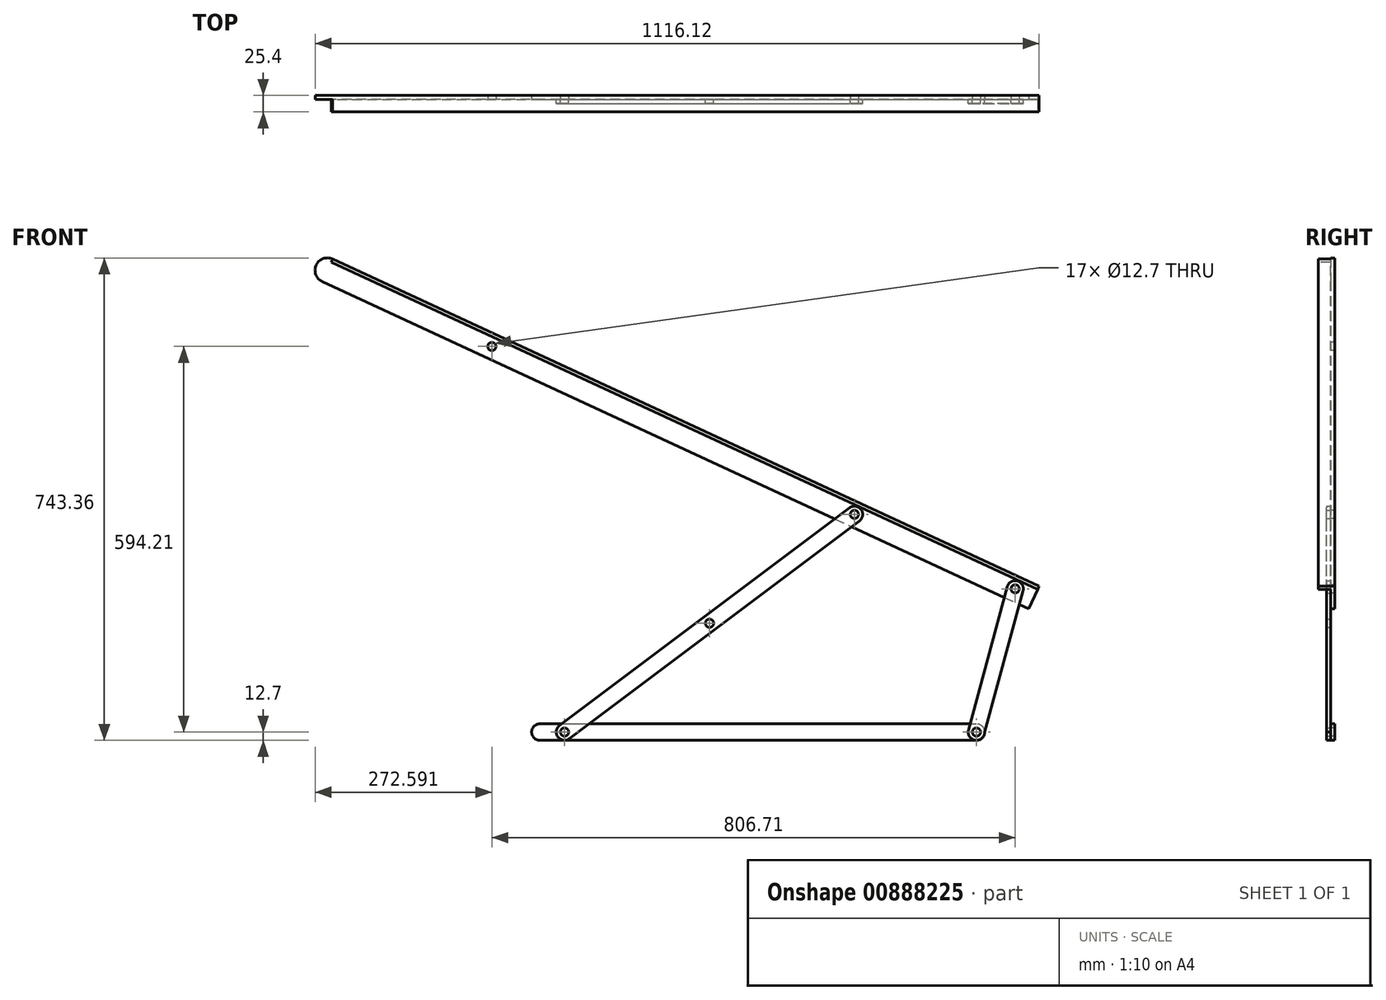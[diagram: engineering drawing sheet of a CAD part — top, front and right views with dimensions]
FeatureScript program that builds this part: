
annotation { "Feature Type Name" : "Feature", "Feature Type Description" : "" }
export const myFeature = defineFeature(function(context is Context, id is Id, definition is map)
    precondition{}
    {
        {
            var Q0;
            Q0=qCreatedBy(makeId("Front.planeOp"),FACE);
            var sketch = newSketch(context, id + "F0", { "sketchPlane" : qUnion([Q0])});
            skCircle(sketch, "E0", {"center": v(0, 0) * mm, "radius": 6.35 * mm});
            skCircle(sketch, "E1", {"center": v(0, 0) * mm, "radius": 12.7 * mm});
            skLineSegment(sketch, "E2", {"start": v(0, 0) * mm, "end": v(-673.1, 0) * mm, "construction": true});
            skCircle(sketch, "E3", {"center": v(-673.1, 0) * mm, "radius": 12.7 * mm});
            skLineSegment(sketch, "E4", {"start": v(-673.1, 12.7) * mm, "end": v(0, 12.7) * mm});
            skLineSegment(sketch, "E5", {"start": v(-673.1, -12.7) * mm, "end": v(0, -12.7) * mm});
            skCircle(sketch, "E6", {"center": v(-635, 0) * mm, "radius": 6.35 * mm});
            skCircle(sketch, "E7", {"center": v(59.73, 220.66) * mm, "radius": 12.7 * mm});
            skCircle(sketch, "E8", {"center": v(-188.04, 335.4) * mm, "radius": 12.7 * mm});
            skCircle(sketch, "E9", {"center": v(-1000.52, 711.61) * mm, "radius": 19.05 * mm});
            skLineSegment(sketch, "E10", {"start": v(-635, 0) * mm, "end": v(-188.04, 335.4) * mm, "construction": true});
            skLineSegment(sketch, "E11", {"start": v(0, 0) * mm, "end": v(59.73, 220.66) * mm, "construction": true});
            skLineSegment(sketch, "E12", {"start": v(59.73, 220.66) * mm, "end": v(-1000.52, 711.61) * mm, "construction": true});
            skCircle(sketch, "E13", {"center": v(-746.98, 594.21) * mm, "radius": 6.35 * mm});
            skCircle(sketch, "E14", {"center": v(-411.52, 167.7) * mm, "radius": 6.35 * mm});
            skCircle(sketch, "E15", {"center": v(-188.04, 335.4) * mm, "radius": 6.35 * mm});
            skCircle(sketch, "E16", {"center": v(59.73, 220.66) * mm, "radius": 6.35 * mm});
            skCircle(sketch, "E17", {"center": v(-635, 0) * mm, "radius": 12.7 * mm});
            skLineSegment(sketch, "E18", {"start": v(-642.62, 10.16) * mm, "end": v(-195.67, 345.55) * mm});
            skLineSegment(sketch, "E19", {"start": v(12.7, 0) * mm, "end": v(71.98, 217.32) * mm});
            skLineSegment(sketch, "E20", {"start": v(47.47, 223.98) * mm, "end": v(-12.26, 3.32) * mm});
            skLineSegment(sketch, "E21", {"start": v(96.55, 224.6) * mm, "end": v(-992.51, 728.9) * mm});
            skLineSegment(sketch, "E22", {"start": v(-1008.52, 694.33) * mm, "end": v(80.54, 190.03) * mm});
            skLineSegment(sketch, "E23", {"start": v(80.54, 190.03) * mm, "end": v(96.55, 224.6) * mm});
            skLineSegment(sketch, "E24", {"start": v(-627.38, -10.16) * mm, "end": v(-180.42, 325.23) * mm});
            skSolve(sketch);
        }
        {
            var Q0;
            {var subQ3=sQuery(id+"F0.wireOp",EDGE,"E5");var subQ5=sQuery(id+"F0.wireOp",EDGE,"E1");var subQ6=makeQuery(id+"F0.imprint","INTERSECT",VERTEX,{"derivedFrom":[subQ5,subQ3]});Q0=makeQuery(id+"F0.imprint","IMPRINT",FACE,{"disambiguationData":[TD([[makeQuery(id+"F0.imprint","IMPRINT",EDGE,{"disambiguationData":[TD([[subQ6,1.0]])],"derivedFrom":subQ5}),-1.0]])]});}
            var Q1;
            {var subQ0=sQuery(id+"F0.wireOp",EDGE,"E3");var subQ1=makeQuery(id+"F0.imprint","INTERSECT",VERTEX,{"derivedFrom":[subQ0,sQuery(id+"F0.wireOp",EDGE,"E4")]});Q1=makeQuery(id+"F0.imprint","IMPRINT",FACE,{"disambiguationData":[TD([[makeQuery(id+"F0.imprint","IMPRINT",EDGE,{"disambiguationData":[TD([[subQ1,-1.0]])],"derivedFrom":subQ0}),1.0]])]});}
            var Q2;
            {var subQ1=sQuery(id+"F0.wireOp",EDGE,"E3");var subQ5=sQuery(id+"F0.wireOp",EDGE,"E4");var subQ8=makeQuery(id+"F0.imprint","INTERSECT",VERTEX,{"derivedFrom":[subQ1,subQ5]});Q2=makeQuery(id+"F0.imprint","IMPRINT",FACE,{"disambiguationData":[TD([[makeQuery(id+"F0.imprint","IMPRINT",EDGE,{"disambiguationData":[TD([[subQ8,1.0]])],"derivedFrom":subQ1}),-1.0]])]});}
            var Q3;
            Q3=makeQuery(id+"F0.imprint","IMPRINT",FACE,{"disambiguationData":[TD([[makeQuery(id+"F0.imprint","IMPRINT",EDGE,{"derivedFrom":sQuery(id+"F0.wireOp",EDGE,"E6")}),-1.0]])]});
            var Q4;
            {var subQ0=sQuery(id+"F0.wireOp",EDGE,"E10");var subQ1=sQuery(id+"F0.wireOp",EDGE,"E4");var subQ2=makeQuery(id+"F0.imprint","INTERSECT",VERTEX,{"derivedFrom":[subQ1,subQ0]});Q4=makeQuery(id+"F0.imprint","IMPRINT",FACE,{"disambiguationData":[TD([[makeQuery(id+"F0.imprint","IMPRINT",EDGE,{"disambiguationData":[TD([[subQ2,-1.0]])],"derivedFrom":subQ1}),-1.0]])]});}
            var Q5;
            {var subQ0=sQuery(id+"F0.wireOp",EDGE,"E17");var subQ1=sQuery(id+"F0.wireOp",EDGE,"E4");var subQ2=makeQuery(id+"F0.imprint","INTERSECT",VERTEX,{"derivedFrom":[subQ1,subQ0]});Q5=makeQuery(id+"F0.imprint","IMPRINT",FACE,{"disambiguationData":[TD([[makeQuery(id+"F0.imprint","IMPRINT",EDGE,{"disambiguationData":[TD([[subQ2,-1.0]])],"derivedFrom":subQ1}),-1.0]])]});}
            var Q6;
            {var subQ0=sQuery(id+"F0.wireOp",EDGE,"E20");var subQ1=sQuery(id+"F0.wireOp",EDGE,"E1");var subQ2=makeQuery(id+"F0.imprint","INTERSECT",VERTEX,{"derivedFrom":[subQ1,subQ0]});Q6=makeQuery(id+"F0.imprint","IMPRINT",FACE,{"disambiguationData":[TD([[makeQuery(id+"F0.imprint","IMPRINT",EDGE,{"disambiguationData":[TD([[subQ2,1.0]])],"derivedFrom":subQ1}),-1.0]])]});}
            var Q7;
            Q7=makeQuery(id+"F0.imprint","IMPRINT",FACE,{"disambiguationData":[TD([[makeQuery(id+"F0.imprint","IMPRINT",EDGE,{"derivedFrom":sQuery(id+"F0.wireOp",EDGE,"E0")}),-1.0]])]});
            var Q8;
            {var subQ0=sQuery(id+"F0.wireOp",EDGE,"E19");var subQ1=sQuery(id+"F0.wireOp",EDGE,"E7");var subQ2=makeQuery(id+"F0.imprint","INTERSECT",VERTEX,{"derivedFrom":[subQ1,subQ0]});Q8=makeQuery(id+"F0.imprint","IMPRINT",FACE,{"disambiguationData":[TD([[makeQuery(id+"F0.imprint","IMPRINT",EDGE,{"disambiguationData":[TD([[subQ2,1.0]])],"derivedFrom":subQ1}),-1.0]])]});}
            var Q9;
            {var subQ0=sQuery(id+"F0.wireOp",EDGE,"E21");Q9=makeQuery(id+"F0.imprint","IMPRINT",FACE,{"disambiguationData":[TD([[makeQuery(id+"F0.imprint","IMPRINT",EDGE,{"derivedFrom":subQ0}),1.0]])]});}
            var Q10;
            {var subQ1=sQuery(id+"F0.wireOp",EDGE,"E7");var subQ5=makeQuery(id+"F0.imprint","INTERSECT",VERTEX,{"derivedFrom":[subQ1,sQuery(id+"F0.wireOp",EDGE,"E19")]});Q10=makeQuery(id+"F0.imprint","IMPRINT",FACE,{"disambiguationData":[TD([[makeQuery(id+"F0.imprint","IMPRINT",EDGE,{"disambiguationData":[TD([[subQ5,-1.0]])],"derivedFrom":subQ1}),1.0]])]});}
            var Q11;
            {var subQ1=sQuery(id+"F0.wireOp",EDGE,"E7");var subQ8=makeQuery(id+"F0.imprint","INTERSECT",VERTEX,{"derivedFrom":[subQ1,sQuery(id+"F0.wireOp",EDGE,"E20")]});Q11=makeQuery(id+"F0.imprint","IMPRINT",FACE,{"disambiguationData":[TD([[makeQuery(id+"F0.imprint","IMPRINT",EDGE,{"disambiguationData":[TD([[subQ8,1.0]])],"derivedFrom":subQ1}),1.0]])]});}
            var Q12;
            {var subQ0=sQuery(id+"F0.wireOp",EDGE,"E20");var subQ1=sQuery(id+"F0.wireOp",EDGE,"E7");var subQ2=makeQuery(id+"F0.imprint","INTERSECT",VERTEX,{"derivedFrom":[subQ1,subQ0]});Q12=makeQuery(id+"F0.imprint","IMPRINT",FACE,{"disambiguationData":[TD([[makeQuery(id+"F0.imprint","IMPRINT",EDGE,{"disambiguationData":[TD([[subQ2,-1.0]])],"derivedFrom":subQ1}),-1.0]])]});}
            var Q13;
            {var subQ0=sQuery(id+"F0.wireOp",EDGE,"E20");var subQ1=sQuery(id+"F0.wireOp",EDGE,"E7");var subQ2=makeQuery(id+"F0.imprint","INTERSECT",VERTEX,{"derivedFrom":[subQ1,subQ0]});Q13=makeQuery(id+"F0.imprint","IMPRINT",FACE,{"disambiguationData":[TD([[makeQuery(id+"F0.imprint","IMPRINT",EDGE,{"disambiguationData":[TD([[subQ2,1.0]])],"derivedFrom":subQ1}),-1.0]])]});}
            var Q14;
            {var subQ1=sQuery(id+"F0.wireOp",EDGE,"E8");var subQ5=makeQuery(id+"F0.imprint","INTERSECT",VERTEX,{"derivedFrom":[subQ1,sQuery(id+"F0.wireOp",EDGE,"E18")]});Q14=makeQuery(id+"F0.imprint","IMPRINT",FACE,{"disambiguationData":[TD([[makeQuery(id+"F0.imprint","IMPRINT",EDGE,{"disambiguationData":[TD([[subQ5,-1.0]])],"derivedFrom":subQ1}),1.0]])]});}
            var Q15;
            {var subQ1=sQuery(id+"F0.wireOp",EDGE,"E8");var subQ8=makeQuery(id+"F0.imprint","INTERSECT",VERTEX,{"derivedFrom":[subQ1,sQuery(id+"F0.wireOp",EDGE,"E24")]});Q15=makeQuery(id+"F0.imprint","IMPRINT",FACE,{"disambiguationData":[TD([[makeQuery(id+"F0.imprint","IMPRINT",EDGE,{"disambiguationData":[TD([[subQ8,1.0]])],"derivedFrom":subQ1}),1.0]])]});}
            var Q16;
            {var subQ0=sQuery(id+"F0.wireOp",EDGE,"E24");var subQ1=sQuery(id+"F0.wireOp",EDGE,"E8");var subQ2=makeQuery(id+"F0.imprint","INTERSECT",VERTEX,{"derivedFrom":[subQ1,subQ0]});Q16=makeQuery(id+"F0.imprint","IMPRINT",FACE,{"disambiguationData":[TD([[makeQuery(id+"F0.imprint","IMPRINT",EDGE,{"disambiguationData":[TD([[subQ2,1.0]])],"derivedFrom":subQ1}),-1.0]])]});}
            var Q17;
            {var subQ3=sQuery(id+"F0.wireOp",EDGE,"E12");var subQ6=sQuery(id+"F0.wireOp",EDGE,"E8");var subQ9=makeQuery(id+"F0.imprint","INTERSECT",VERTEX,{"disambiguationData":[OD(0.0)],"derivedFrom":[subQ6,subQ3]});Q17=makeQuery(id+"F0.imprint","IMPRINT",FACE,{"disambiguationData":[TD([[makeQuery(id+"F0.imprint","IMPRINT",EDGE,{"disambiguationData":[TD([[subQ9,-1.0]])],"derivedFrom":subQ6}),-1.0]])]});}
            var Q18;
            {var subQ0=sQuery(id+"F0.wireOp",EDGE,"E12");var subQ1=sQuery(id+"F0.wireOp",EDGE,"E8");var subQ2=makeQuery(id+"F0.imprint","INTERSECT",VERTEX,{"disambiguationData":[OD(0.0)],"derivedFrom":[subQ1,subQ0]});Q18=makeQuery(id+"F0.imprint","IMPRINT",FACE,{"disambiguationData":[TD([[makeQuery(id+"F0.imprint","IMPRINT",EDGE,{"disambiguationData":[TD([[subQ2,-1.0]])],"derivedFrom":subQ1}),1.0]])]});}
            var Q19;
            {var subQ1=sQuery(id+"F0.wireOp",EDGE,"E9");var subQ8=sQuery(id+"F0.wireOp",EDGE,"E22");var subQ9=makeQuery(id+"F0.imprint","INTERSECT",VERTEX,{"derivedFrom":[subQ1,subQ8]});Q19=makeQuery(id+"F0.imprint","IMPRINT",FACE,{"disambiguationData":[TD([[makeQuery(id+"F0.imprint","IMPRINT",EDGE,{"disambiguationData":[TD([[subQ9,-1.0]])],"derivedFrom":subQ1}),-1.0]])]});}
            var Q20;
            {var subQ0=sQuery(id+"F0.wireOp",EDGE,"E9");var subQ1=makeQuery(id+"F0.imprint","INTERSECT",VERTEX,{"derivedFrom":[subQ0,sQuery(id+"F0.wireOp",EDGE,"E21")]});Q20=makeQuery(id+"F0.imprint","IMPRINT",FACE,{"disambiguationData":[TD([[makeQuery(id+"F0.imprint","IMPRINT",EDGE,{"disambiguationData":[TD([[subQ1,-1.0]])],"derivedFrom":subQ0}),1.0]])]});}
            var Q21;
            {var subQ0=sQuery(id+"F0.wireOp",EDGE,"E18");var subQ1=sQuery(id+"F0.wireOp",EDGE,"E4");var subQ2=makeQuery(id+"F0.imprint","INTERSECT",VERTEX,{"derivedFrom":[subQ1,subQ0]});Q21=makeQuery(id+"F0.imprint","IMPRINT",FACE,{"disambiguationData":[TD([[makeQuery(id+"F0.imprint","IMPRINT",EDGE,{"disambiguationData":[TD([[subQ2,-1.0]])],"derivedFrom":subQ1}),-1.0]])]});}
            var Q22;
            {var subQ0=sQuery(id+"F0.wireOp",EDGE,"E18");var subQ1=sQuery(id+"F0.wireOp",EDGE,"E8");var subQ2=makeQuery(id+"F0.imprint","INTERSECT",VERTEX,{"derivedFrom":[subQ1,subQ0]});Q22=makeQuery(id+"F0.imprint","IMPRINT",FACE,{"disambiguationData":[TD([[makeQuery(id+"F0.imprint","IMPRINT",EDGE,{"disambiguationData":[TD([[subQ2,-1.0]])],"derivedFrom":subQ1}),-1.0]])]});}
            extrude(context, id + "F1", {"entities" : qUnion([Q0, Q1, Q2, Q3, Q4, Q5, Q6, Q7, Q8, Q9, Q10, Q11, Q12, Q13, Q14, Q15, Q16, Q17, Q18, Q19, Q20, Q21, Q22]), "oppositeDirection" : true, "depth" : 6.35 * mm, "offsetDistance" : 25.4 * mm});
        }
        {
            var Q0;
            {var subQ0=sQuery(id+"F0.wireOp",EDGE,"E10");var subQ1=sQuery(id+"F0.wireOp",EDGE,"E4");var subQ2=makeQuery(id+"F0.imprint","INTERSECT",VERTEX,{"derivedFrom":[subQ1,subQ0]});Q0=makeQuery(id+"F0.imprint","IMPRINT",FACE,{"disambiguationData":[TD([[makeQuery(id+"F0.imprint","IMPRINT",EDGE,{"disambiguationData":[TD([[subQ2,-1.0]])],"derivedFrom":subQ1}),-1.0]])]});}
            var Q1;
            Q1=makeQuery(id+"F0.imprint","IMPRINT",FACE,{"disambiguationData":[TD([[makeQuery(id+"F0.imprint","IMPRINT",EDGE,{"derivedFrom":sQuery(id+"F0.wireOp",EDGE,"E6")}),-1.0]])]});
            var Q2;
            {var subQ6=sQuery(id+"F0.wireOp",EDGE,"E18");var subQ7=sQuery(id+"F0.wireOp",EDGE,"E4");var subQ8=makeQuery(id+"F0.imprint","INTERSECT",VERTEX,{"derivedFrom":[subQ7,subQ6]});Q2=makeQuery(id+"F0.imprint","IMPRINT",FACE,{"disambiguationData":[TD([[makeQuery(id+"F0.imprint","IMPRINT",EDGE,{"disambiguationData":[TD([[subQ8,-1.0]])],"derivedFrom":subQ7}),1.0]])]});}
            var Q3;
            {var subQ1=sQuery(id+"F0.wireOp",EDGE,"E10");var subQ5=sQuery(id+"F0.wireOp",EDGE,"E4");var subQ6=makeQuery(id+"F0.imprint","INTERSECT",VERTEX,{"derivedFrom":[subQ5,subQ1]});Q3=makeQuery(id+"F0.imprint","IMPRINT",FACE,{"disambiguationData":[TD([[makeQuery(id+"F0.imprint","IMPRINT",EDGE,{"disambiguationData":[TD([[subQ6,-1.0]])],"derivedFrom":subQ5}),1.0]])]});}
            var Q4;
            {var subQ0=sQuery(id+"F0.wireOp",EDGE,"E24");var subQ1=sQuery(id+"F0.wireOp",EDGE,"E8");var subQ2=makeQuery(id+"F0.imprint","INTERSECT",VERTEX,{"derivedFrom":[subQ1,subQ0]});Q4=makeQuery(id+"F0.imprint","IMPRINT",FACE,{"disambiguationData":[TD([[makeQuery(id+"F0.imprint","IMPRINT",EDGE,{"disambiguationData":[TD([[subQ2,1.0]])],"derivedFrom":subQ1}),-1.0]])]});}
            var Q5;
            {var subQ3=sQuery(id+"F0.wireOp",EDGE,"E12");var subQ6=sQuery(id+"F0.wireOp",EDGE,"E8");var subQ9=makeQuery(id+"F0.imprint","INTERSECT",VERTEX,{"disambiguationData":[OD(0.0)],"derivedFrom":[subQ6,subQ3]});Q5=makeQuery(id+"F0.imprint","IMPRINT",FACE,{"disambiguationData":[TD([[makeQuery(id+"F0.imprint","IMPRINT",EDGE,{"disambiguationData":[TD([[subQ9,-1.0]])],"derivedFrom":subQ6}),-1.0]])]});}
            var Q6;
            {var subQ1=sQuery(id+"F0.wireOp",EDGE,"E8");var subQ5=makeQuery(id+"F0.imprint","INTERSECT",VERTEX,{"derivedFrom":[subQ1,sQuery(id+"F0.wireOp",EDGE,"E18")]});Q6=makeQuery(id+"F0.imprint","IMPRINT",FACE,{"disambiguationData":[TD([[makeQuery(id+"F0.imprint","IMPRINT",EDGE,{"disambiguationData":[TD([[subQ5,-1.0]])],"derivedFrom":subQ1}),1.0]])]});}
            var Q7;
            {var subQ1=sQuery(id+"F0.wireOp",EDGE,"E8");var subQ8=makeQuery(id+"F0.imprint","INTERSECT",VERTEX,{"derivedFrom":[subQ1,sQuery(id+"F0.wireOp",EDGE,"E24")]});Q7=makeQuery(id+"F0.imprint","IMPRINT",FACE,{"disambiguationData":[TD([[makeQuery(id+"F0.imprint","IMPRINT",EDGE,{"disambiguationData":[TD([[subQ8,1.0]])],"derivedFrom":subQ1}),1.0]])]});}
            var Q8;
            {var subQ0=sQuery(id+"F0.wireOp",EDGE,"E12");var subQ1=sQuery(id+"F0.wireOp",EDGE,"E8");var subQ2=makeQuery(id+"F0.imprint","INTERSECT",VERTEX,{"disambiguationData":[OD(0.0)],"derivedFrom":[subQ1,subQ0]});Q8=makeQuery(id+"F0.imprint","IMPRINT",FACE,{"disambiguationData":[TD([[makeQuery(id+"F0.imprint","IMPRINT",EDGE,{"disambiguationData":[TD([[subQ2,-1.0]])],"derivedFrom":subQ1}),1.0]])]});}
            var Q9;
            {var subQ0=sQuery(id+"F0.wireOp",EDGE,"E18");var subQ1=sQuery(id+"F0.wireOp",EDGE,"E8");var subQ2=makeQuery(id+"F0.imprint","INTERSECT",VERTEX,{"derivedFrom":[subQ1,subQ0]});Q9=makeQuery(id+"F0.imprint","IMPRINT",FACE,{"disambiguationData":[TD([[makeQuery(id+"F0.imprint","IMPRINT",EDGE,{"disambiguationData":[TD([[subQ2,-1.0]])],"derivedFrom":subQ1}),-1.0]])]});}
            var Q10;
            {var subQ1=sQuery(id+"F0.wireOp",EDGE,"E7");var subQ5=makeQuery(id+"F0.imprint","INTERSECT",VERTEX,{"derivedFrom":[subQ1,sQuery(id+"F0.wireOp",EDGE,"E19")]});Q10=makeQuery(id+"F0.imprint","IMPRINT",FACE,{"disambiguationData":[TD([[makeQuery(id+"F0.imprint","IMPRINT",EDGE,{"disambiguationData":[TD([[subQ5,-1.0]])],"derivedFrom":subQ1}),1.0]])]});}
            var Q11;
            {var subQ1=sQuery(id+"F0.wireOp",EDGE,"E7");var subQ8=makeQuery(id+"F0.imprint","INTERSECT",VERTEX,{"derivedFrom":[subQ1,sQuery(id+"F0.wireOp",EDGE,"E20")]});Q11=makeQuery(id+"F0.imprint","IMPRINT",FACE,{"disambiguationData":[TD([[makeQuery(id+"F0.imprint","IMPRINT",EDGE,{"disambiguationData":[TD([[subQ8,1.0]])],"derivedFrom":subQ1}),1.0]])]});}
            var Q12;
            {var subQ0=sQuery(id+"F0.wireOp",EDGE,"E20");var subQ1=sQuery(id+"F0.wireOp",EDGE,"E7");var subQ2=makeQuery(id+"F0.imprint","INTERSECT",VERTEX,{"derivedFrom":[subQ1,subQ0]});Q12=makeQuery(id+"F0.imprint","IMPRINT",FACE,{"disambiguationData":[TD([[makeQuery(id+"F0.imprint","IMPRINT",EDGE,{"disambiguationData":[TD([[subQ2,-1.0]])],"derivedFrom":subQ1}),-1.0]])]});}
            var Q13;
            {var subQ0=sQuery(id+"F0.wireOp",EDGE,"E19");var subQ1=sQuery(id+"F0.wireOp",EDGE,"E7");var subQ2=makeQuery(id+"F0.imprint","INTERSECT",VERTEX,{"derivedFrom":[subQ1,subQ0]});Q13=makeQuery(id+"F0.imprint","IMPRINT",FACE,{"disambiguationData":[TD([[makeQuery(id+"F0.imprint","IMPRINT",EDGE,{"disambiguationData":[TD([[subQ2,1.0]])],"derivedFrom":subQ1}),-1.0]])]});}
            var Q14;
            {var subQ0=sQuery(id+"F0.wireOp",EDGE,"E20");var subQ1=sQuery(id+"F0.wireOp",EDGE,"E4");var subQ2=makeQuery(id+"F0.imprint","INTERSECT",VERTEX,{"derivedFrom":[subQ1,subQ0]});Q14=makeQuery(id+"F0.imprint","IMPRINT",FACE,{"disambiguationData":[TD([[makeQuery(id+"F0.imprint","IMPRINT",EDGE,{"disambiguationData":[TD([[subQ2,-1.0]])],"derivedFrom":subQ1}),1.0]])]});}
            var Q15;
            {var subQ1=sQuery(id+"F0.wireOp",EDGE,"E4");var subQ5=sQuery(id+"F0.wireOp",EDGE,"E1");var subQ6=makeQuery(id+"F0.imprint","INTERSECT",VERTEX,{"derivedFrom":[subQ5,subQ1]});Q15=makeQuery(id+"F0.imprint","IMPRINT",FACE,{"disambiguationData":[TD([[makeQuery(id+"F0.imprint","IMPRINT",EDGE,{"disambiguationData":[TD([[subQ6,1.0]])],"derivedFrom":subQ5}),-1.0]])]});}
            var Q16;
            {var subQ0=sQuery(id+"F0.wireOp",EDGE,"E20");var subQ1=sQuery(id+"F0.wireOp",EDGE,"E1");var subQ2=makeQuery(id+"F0.imprint","INTERSECT",VERTEX,{"derivedFrom":[subQ1,subQ0]});Q16=makeQuery(id+"F0.imprint","IMPRINT",FACE,{"disambiguationData":[TD([[makeQuery(id+"F0.imprint","IMPRINT",EDGE,{"disambiguationData":[TD([[subQ2,1.0]])],"derivedFrom":subQ1}),-1.0]])]});}
            var Q17;
            Q17=makeQuery(id+"F0.imprint","IMPRINT",FACE,{"disambiguationData":[TD([[makeQuery(id+"F0.imprint","IMPRINT",EDGE,{"derivedFrom":sQuery(id+"F0.wireOp",EDGE,"E0")}),-1.0]])]});
            var Q18;
            {var subQ0=sQuery(id+"F0.wireOp",EDGE,"E17");var subQ1=sQuery(id+"F0.wireOp",EDGE,"E4");var subQ2=makeQuery(id+"F0.imprint","INTERSECT",VERTEX,{"disambiguationData":[OD(1.0)],"derivedFrom":[subQ1,subQ0]});Q18=makeQuery(id+"F0.imprint","IMPRINT",FACE,{"disambiguationData":[TD([[makeQuery(id+"F0.imprint","IMPRINT",EDGE,{"disambiguationData":[TD([[subQ2,-1.0]])],"derivedFrom":subQ1}),-1.0]])]});}
            var Q19;
            {var subQ0=sQuery(id+"F0.wireOp",EDGE,"E17");var subQ1=sQuery(id+"F0.wireOp",EDGE,"E4");var subQ2=makeQuery(id+"F0.imprint","INTERSECT",VERTEX,{"disambiguationData":[OD(0.0)],"derivedFrom":[subQ1,subQ0]});Q19=makeQuery(id+"F0.imprint","IMPRINT",FACE,{"disambiguationData":[TD([[makeQuery(id+"F0.imprint","IMPRINT",EDGE,{"disambiguationData":[TD([[subQ2,-1.0]])],"derivedFrom":subQ1}),1.0]])]});}
            var Q20;
            {var subQ0=sQuery(id+"F0.wireOp",EDGE,"E18");var subQ1=sQuery(id+"F0.wireOp",EDGE,"E4");var subQ2=makeQuery(id+"F0.imprint","INTERSECT",VERTEX,{"derivedFrom":[subQ1,subQ0]});Q20=makeQuery(id+"F0.imprint","IMPRINT",FACE,{"disambiguationData":[TD([[makeQuery(id+"F0.imprint","IMPRINT",EDGE,{"disambiguationData":[TD([[subQ2,-1.0]])],"derivedFrom":subQ1}),-1.0]])]});}
            extrude(context, id + "F2", {"entities" : qUnion([Q0, Q1, Q2, Q3, Q4, Q5, Q6, Q7, Q8, Q9, Q10, Q11, Q12, Q13, Q14, Q15, Q16, Q17, Q18, Q19, Q20]), "depth" : 6.35 * mm, "offsetDistance" : 25.4 * mm});
        }
        {
            var Q0;
            Q0=makeQuery(id+"F1.opExtrude","SWEPT_FACE",FACE,{"disambiguationData":[OSD([sQuery(id+"F0.wireOp",EDGE,"E21")])]});
            var sketch = newSketch(context, id + "F3", { "sketchPlane" : qUnion([Q0])});
            skLineSegment(sketch, "E25.bottom", {"start": v(-6.77, 6.35) * mm, "end": v(-1206.92, 6.35) * mm});
            skLineSegment(sketch, "E25.top", {"start": v(-6.77, -19.05) * mm, "end": v(-1206.92, -19.05) * mm});
            skLineSegment(sketch, "E25.left", {"start": v(-6.77, 6.35) * mm, "end": v(-6.77, -19.05) * mm});
            skLineSegment(sketch, "E25.right", {"start": v(-1206.92, 6.35) * mm, "end": v(-1206.92, -19.05) * mm});
            skSolve(sketch);
        }
        {
            var Q0;
            {var subQ0=sQuery(id+"F3.wireOp",EDGE,"E25.top");Q0=makeQuery(id+"F3.imprint","IMPRINT",FACE,{"disambiguationData":[TD([[makeQuery(id+"F3.imprint","IMPRINT",EDGE,{"derivedFrom":subQ0}),-1.0]])]});}
            var Q1;
            {var subQ0=sQuery(id+"F3.wireOp",EDGE,"E25.bottom");Q1=makeQuery(id+"F3.imprint","IMPRINT",FACE,{"disambiguationData":[TD([[makeQuery(id+"F3.imprint","IMPRINT",EDGE,{"derivedFrom":subQ0}),1.0]])]});}
            extrude(context, id + "F4", {"entities" : qUnion([Q0, Q1]), "operationType" : NewBodyOperationType.ADD, "oppositeDirection" : true, "depth" : 5.08 * mm, "offsetDistance" : 25.4 * mm});
        }
    });
